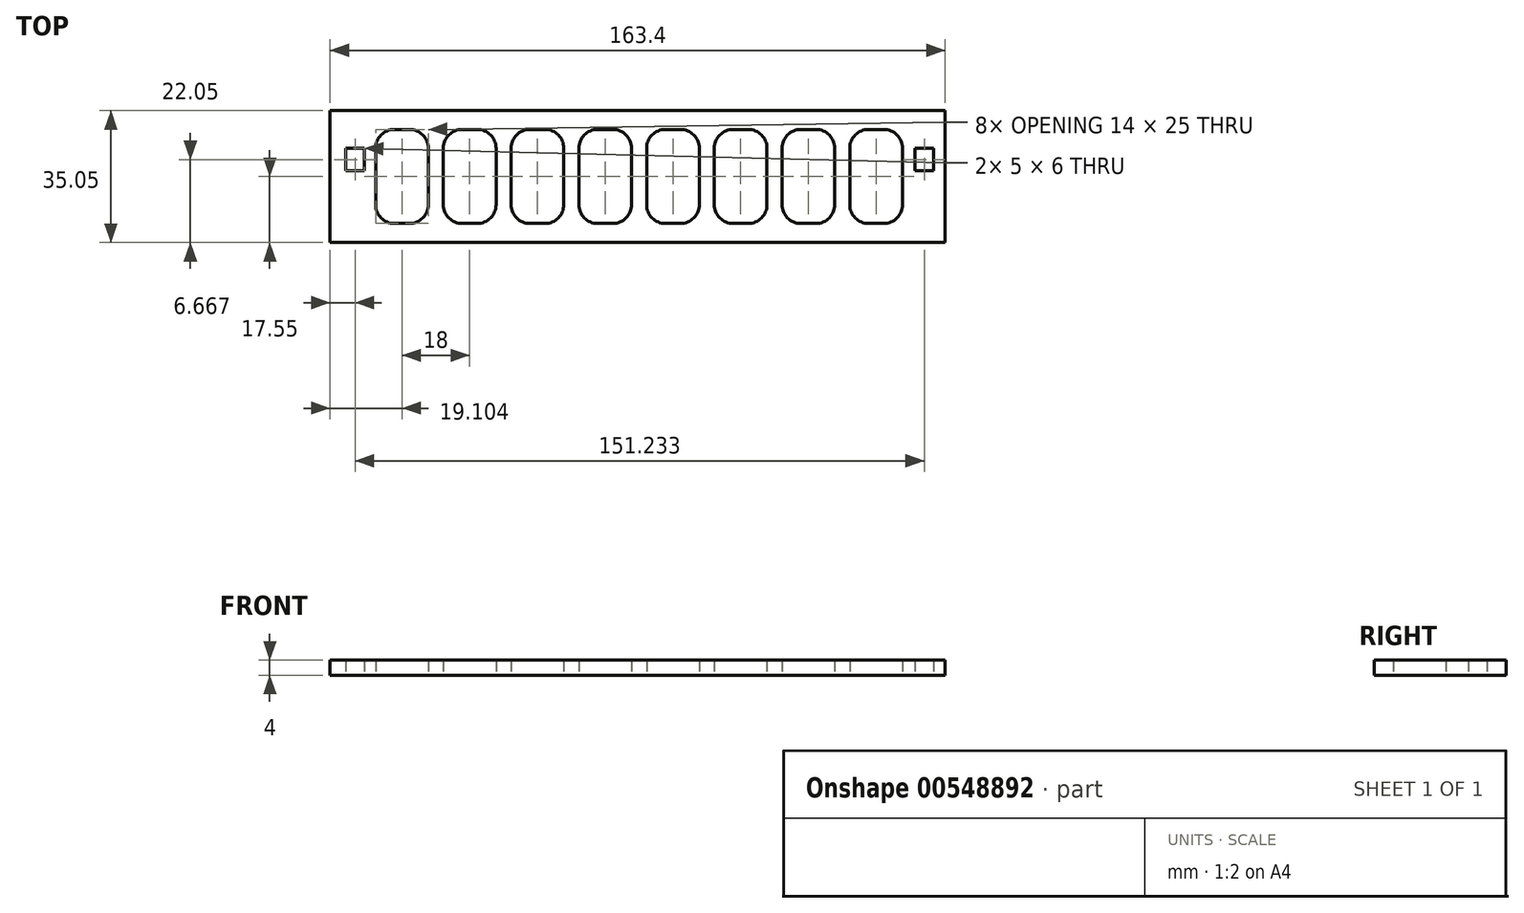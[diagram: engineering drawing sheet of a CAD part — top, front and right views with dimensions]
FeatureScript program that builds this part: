
annotation { "Feature Type Name" : "Feature", "Feature Type Description" : "" }
export const myFeature = defineFeature(function(context is Context, id is Id, definition is map)
    precondition{}
    {
        {
            var Q0;
            Q0=qCreatedBy(makeId("Top.planeOp"),FACE);
            var sketch = newSketch(context, id + "F0", { "sketchPlane" : qUnion([Q0])});
            skLineSegment(sketch, "E0.bottom", {"start": v(21.1, 30.05) * mm, "end": v(17.1, 30.05) * mm});
            skLineSegment(sketch, "E0.top", {"start": v(21.1, 5.05) * mm, "end": v(17.1, 5.05) * mm});
            skLineSegment(sketch, "E0.left", {"start": v(26.1, 25.05) * mm, "end": v(26.1, 10.05) * mm});
            skLineSegment(sketch, "E0.right", {"start": v(12.1, 25.05) * mm, "end": v(12.1, 10.05) * mm});
            skPoint(sketch, "E0.middle", {"position": v(19.1, 17.55) * mm});
            skLineSegment(sketch, "E1.bottom", {"start": v(0, 0) * mm, "end": v(163.4, 0) * mm});
            skLineSegment(sketch, "E1.top", {"start": v(0, 35.05) * mm, "end": v(163.4, 35.05) * mm});
            skLineSegment(sketch, "E1.left", {"start": v(0, 0) * mm, "end": v(0, 35.05) * mm});
            skLineSegment(sketch, "E1.right", {"start": v(163.4, 0) * mm, "end": v(163.4, 35.05) * mm});
            skPoint(sketch, "E2.visualSharp", {"position": v(26.1, 30.05) * mm});
            skArc(sketch, "E2.filletArc", {"start": v(26.1, 25.05) * mm, "mid": v(24.64, 28.59) * mm, "end": v(21.1, 30.05) * mm});
            skPoint(sketch, "E3.visualSharp", {"position": v(26.1, 5.05) * mm});
            skArc(sketch, "E3.filletArc", {"start": v(21.1, 5.05) * mm, "mid": v(24.64, 6.51) * mm, "end": v(26.1, 10.05) * mm});
            skPoint(sketch, "E4.visualSharp", {"position": v(12.1, 5.05) * mm});
            skArc(sketch, "E4.filletArc", {"start": v(12.1, 10.05) * mm, "mid": v(13.57, 6.51) * mm, "end": v(17.1, 5.05) * mm});
            skPoint(sketch, "E5.visualSharp", {"position": v(12.1, 30.05) * mm});
            skArc(sketch, "E5.filletArc", {"start": v(17.1, 30.05) * mm, "mid": v(13.57, 28.59) * mm, "end": v(12.1, 25.05) * mm});
            skPoint(sketch, "E6.1.0.0", {"position": v(37.1, 17.55) * mm});
            skLineSegment(sketch, "E6.1.0.1", {"start": v(44.1, 25.05) * mm, "end": v(44.1, 10.05) * mm});
            skArc(sketch, "E6.1.0.2", {"start": v(44.1, 25.05) * mm, "mid": v(42.64, 28.59) * mm, "end": v(39.1, 30.05) * mm});
            skLineSegment(sketch, "E6.1.0.3", {"start": v(39.1, 30.05) * mm, "end": v(35.1, 30.05) * mm});
            skArc(sketch, "E6.1.0.4", {"start": v(35.1, 30.05) * mm, "mid": v(31.57, 28.59) * mm, "end": v(30.1, 25.05) * mm});
            skLineSegment(sketch, "E6.1.0.5", {"start": v(30.1, 25.05) * mm, "end": v(30.1, 10.05) * mm});
            skArc(sketch, "E6.1.0.6", {"start": v(30.1, 10.05) * mm, "mid": v(31.57, 6.51) * mm, "end": v(35.1, 5.05) * mm});
            skLineSegment(sketch, "E6.1.0.7", {"start": v(39.1, 5.05) * mm, "end": v(35.1, 5.05) * mm});
            skArc(sketch, "E6.1.0.8", {"start": v(39.1, 5.05) * mm, "mid": v(42.64, 6.51) * mm, "end": v(44.1, 10.05) * mm});
            skPoint(sketch, "E6.2.0.0", {"position": v(55.1, 17.55) * mm});
            skLineSegment(sketch, "E6.2.0.1", {"start": v(62.1, 25.05) * mm, "end": v(62.1, 10.05) * mm});
            skArc(sketch, "E6.2.0.2", {"start": v(62.1, 25.05) * mm, "mid": v(60.64, 28.59) * mm, "end": v(57.1, 30.05) * mm});
            skLineSegment(sketch, "E6.2.0.3", {"start": v(57.1, 30.05) * mm, "end": v(53.1, 30.05) * mm});
            skArc(sketch, "E6.2.0.4", {"start": v(53.1, 30.05) * mm, "mid": v(49.57, 28.59) * mm, "end": v(48.1, 25.05) * mm});
            skLineSegment(sketch, "E6.2.0.5", {"start": v(48.1, 25.05) * mm, "end": v(48.1, 10.05) * mm});
            skArc(sketch, "E6.2.0.6", {"start": v(48.1, 10.05) * mm, "mid": v(49.57, 6.51) * mm, "end": v(53.1, 5.05) * mm});
            skLineSegment(sketch, "E6.2.0.7", {"start": v(57.1, 5.05) * mm, "end": v(53.1, 5.05) * mm});
            skArc(sketch, "E6.2.0.8", {"start": v(57.1, 5.05) * mm, "mid": v(60.64, 6.51) * mm, "end": v(62.1, 10.05) * mm});
            skPoint(sketch, "E6.3.0.0", {"position": v(73.1, 17.55) * mm});
            skLineSegment(sketch, "E6.3.0.1", {"start": v(80.1, 25.05) * mm, "end": v(80.1, 10.05) * mm});
            skArc(sketch, "E6.3.0.2", {"start": v(80.1, 25.05) * mm, "mid": v(78.64, 28.59) * mm, "end": v(75.1, 30.05) * mm});
            skLineSegment(sketch, "E6.3.0.3", {"start": v(75.1, 30.05) * mm, "end": v(71.1, 30.05) * mm});
            skArc(sketch, "E6.3.0.4", {"start": v(71.1, 30.05) * mm, "mid": v(67.57, 28.59) * mm, "end": v(66.1, 25.05) * mm});
            skLineSegment(sketch, "E6.3.0.5", {"start": v(66.1, 25.05) * mm, "end": v(66.1, 10.05) * mm});
            skArc(sketch, "E6.3.0.6", {"start": v(66.1, 10.05) * mm, "mid": v(67.57, 6.51) * mm, "end": v(71.1, 5.05) * mm});
            skLineSegment(sketch, "E6.3.0.7", {"start": v(75.1, 5.05) * mm, "end": v(71.1, 5.05) * mm});
            skArc(sketch, "E6.3.0.8", {"start": v(75.1, 5.05) * mm, "mid": v(78.64, 6.51) * mm, "end": v(80.1, 10.05) * mm});
            skPoint(sketch, "E6.4.0.0", {"position": v(91.1, 17.55) * mm});
            skLineSegment(sketch, "E6.4.0.1", {"start": v(98.1, 25.05) * mm, "end": v(98.1, 10.05) * mm});
            skArc(sketch, "E6.4.0.2", {"start": v(98.1, 25.05) * mm, "mid": v(96.64, 28.59) * mm, "end": v(93.1, 30.05) * mm});
            skLineSegment(sketch, "E6.4.0.3", {"start": v(93.1, 30.05) * mm, "end": v(89.1, 30.05) * mm});
            skArc(sketch, "E6.4.0.4", {"start": v(89.1, 30.05) * mm, "mid": v(85.57, 28.59) * mm, "end": v(84.1, 25.05) * mm});
            skLineSegment(sketch, "E6.4.0.5", {"start": v(84.1, 25.05) * mm, "end": v(84.1, 10.05) * mm});
            skArc(sketch, "E6.4.0.6", {"start": v(84.1, 10.05) * mm, "mid": v(85.57, 6.51) * mm, "end": v(89.1, 5.05) * mm});
            skLineSegment(sketch, "E6.4.0.7", {"start": v(93.1, 5.05) * mm, "end": v(89.1, 5.05) * mm});
            skArc(sketch, "E6.4.0.8", {"start": v(93.1, 5.05) * mm, "mid": v(96.64, 6.51) * mm, "end": v(98.1, 10.05) * mm});
            skPoint(sketch, "E6.5.0.0", {"position": v(109.1, 17.55) * mm});
            skLineSegment(sketch, "E6.5.0.1", {"start": v(116.1, 25.05) * mm, "end": v(116.1, 10.05) * mm});
            skArc(sketch, "E6.5.0.2", {"start": v(116.1, 25.05) * mm, "mid": v(114.64, 28.59) * mm, "end": v(111.1, 30.05) * mm});
            skLineSegment(sketch, "E6.5.0.3", {"start": v(111.1, 30.05) * mm, "end": v(107.1, 30.05) * mm});
            skArc(sketch, "E6.5.0.4", {"start": v(107.1, 30.05) * mm, "mid": v(103.57, 28.59) * mm, "end": v(102.1, 25.05) * mm});
            skLineSegment(sketch, "E6.5.0.5", {"start": v(102.1, 25.05) * mm, "end": v(102.1, 10.05) * mm});
            skArc(sketch, "E6.5.0.6", {"start": v(102.1, 10.05) * mm, "mid": v(103.57, 6.51) * mm, "end": v(107.1, 5.05) * mm});
            skLineSegment(sketch, "E6.5.0.7", {"start": v(111.1, 5.05) * mm, "end": v(107.1, 5.05) * mm});
            skArc(sketch, "E6.5.0.8", {"start": v(111.1, 5.05) * mm, "mid": v(114.64, 6.51) * mm, "end": v(116.1, 10.05) * mm});
            skPoint(sketch, "E6.6.0.0", {"position": v(127.1, 17.55) * mm});
            skLineSegment(sketch, "E6.6.0.1", {"start": v(134.1, 25.05) * mm, "end": v(134.1, 10.05) * mm});
            skArc(sketch, "E6.6.0.2", {"start": v(134.1, 25.05) * mm, "mid": v(132.64, 28.59) * mm, "end": v(129.1, 30.05) * mm});
            skLineSegment(sketch, "E6.6.0.3", {"start": v(129.1, 30.05) * mm, "end": v(125.1, 30.05) * mm});
            skArc(sketch, "E6.6.0.4", {"start": v(125.1, 30.05) * mm, "mid": v(121.57, 28.59) * mm, "end": v(120.1, 25.05) * mm});
            skLineSegment(sketch, "E6.6.0.5", {"start": v(120.1, 25.05) * mm, "end": v(120.1, 10.05) * mm});
            skArc(sketch, "E6.6.0.6", {"start": v(120.1, 10.05) * mm, "mid": v(121.57, 6.51) * mm, "end": v(125.1, 5.05) * mm});
            skLineSegment(sketch, "E6.6.0.7", {"start": v(129.1, 5.05) * mm, "end": v(125.1, 5.05) * mm});
            skArc(sketch, "E6.6.0.8", {"start": v(129.1, 5.05) * mm, "mid": v(132.64, 6.51) * mm, "end": v(134.1, 10.05) * mm});
            skLineSegment(sketch, "E6.direction1", {"start": v(19.1, 17.55) * mm, "end": v(37.1, 17.55) * mm, "construction": true});
            skPoint(sketch, "E7.firstSnap0", {"position": v(132.64, 28.59) * mm});
            skLineSegment(sketch, "E8.bottom", {"start": v(155.4, 25.05) * mm, "end": v(160.4, 25.05) * mm});
            skLineSegment(sketch, "E8.top", {"start": v(155.4, 19.05) * mm, "end": v(160.4, 19.05) * mm});
            skLineSegment(sketch, "E8.left", {"start": v(155.4, 25.05) * mm, "end": v(155.4, 19.05) * mm});
            skLineSegment(sketch, "E8.right", {"start": v(160.4, 25.05) * mm, "end": v(160.4, 19.05) * mm});
            skPoint(sketch, "E8.middle", {"position": v(157.9, 22.05) * mm});
            skPoint(sketch, "E9.0.7.0", {"position": v(145.1, 17.55) * mm});
            skLineSegment(sketch, "E9.1.7.0", {"start": v(152.1, 25.05) * mm, "end": v(152.1, 10.05) * mm});
            skArc(sketch, "E9.4.7.0", {"start": v(152.1, 25.05) * mm, "mid": v(150.64, 28.59) * mm, "end": v(147.1, 30.05) * mm});
            skLineSegment(sketch, "E9.8.7.0", {"start": v(147.1, 30.05) * mm, "end": v(143.1, 30.05) * mm});
            skArc(sketch, "E9.11.7.0", {"start": v(143.1, 30.05) * mm, "mid": v(139.57, 28.59) * mm, "end": v(138.1, 25.05) * mm});
            skLineSegment(sketch, "E9.15.7.0", {"start": v(138.1, 25.05) * mm, "end": v(138.1, 10.05) * mm});
            skArc(sketch, "E9.18.7.0", {"start": v(138.1, 10.05) * mm, "mid": v(139.57, 6.51) * mm, "end": v(143.1, 5.05) * mm});
            skLineSegment(sketch, "E9.22.7.0", {"start": v(147.1, 5.05) * mm, "end": v(143.1, 5.05) * mm});
            skArc(sketch, "E9.25.7.0", {"start": v(147.1, 5.05) * mm, "mid": v(150.64, 6.51) * mm, "end": v(152.1, 10.05) * mm});
            skLineSegment(sketch, "E10.bottom", {"start": v(4.17, 25.05) * mm, "end": v(9.17, 25.05) * mm});
            skLineSegment(sketch, "E10.top", {"start": v(4.17, 19.05) * mm, "end": v(9.17, 19.05) * mm});
            skLineSegment(sketch, "E10.left", {"start": v(4.17, 25.05) * mm, "end": v(4.17, 19.05) * mm});
            skLineSegment(sketch, "E10.right", {"start": v(9.17, 25.05) * mm, "end": v(9.17, 19.05) * mm});
            skPoint(sketch, "E10.middle", {"position": v(6.67, 22.05) * mm});
            skSolve(sketch);
        }
        {
            var Q0;
            Q0=makeQuery(id+"F0.imprint","IMPRINT",FACE,{"disambiguationData":[TD([[makeQuery(id+"F0.imprint","IMPRINT",EDGE,{"derivedFrom":sQuery(id+"F0.wireOp",EDGE,"E0.bottom")}),-1.0]])]});
            extrude(context, id + "F1", {"entities" : qUnion([Q0]), "endBound" : BoundingType.SYMMETRIC, "depth" : 4 * mm, "offsetDistance" : 25 * mm});
        }
    });
